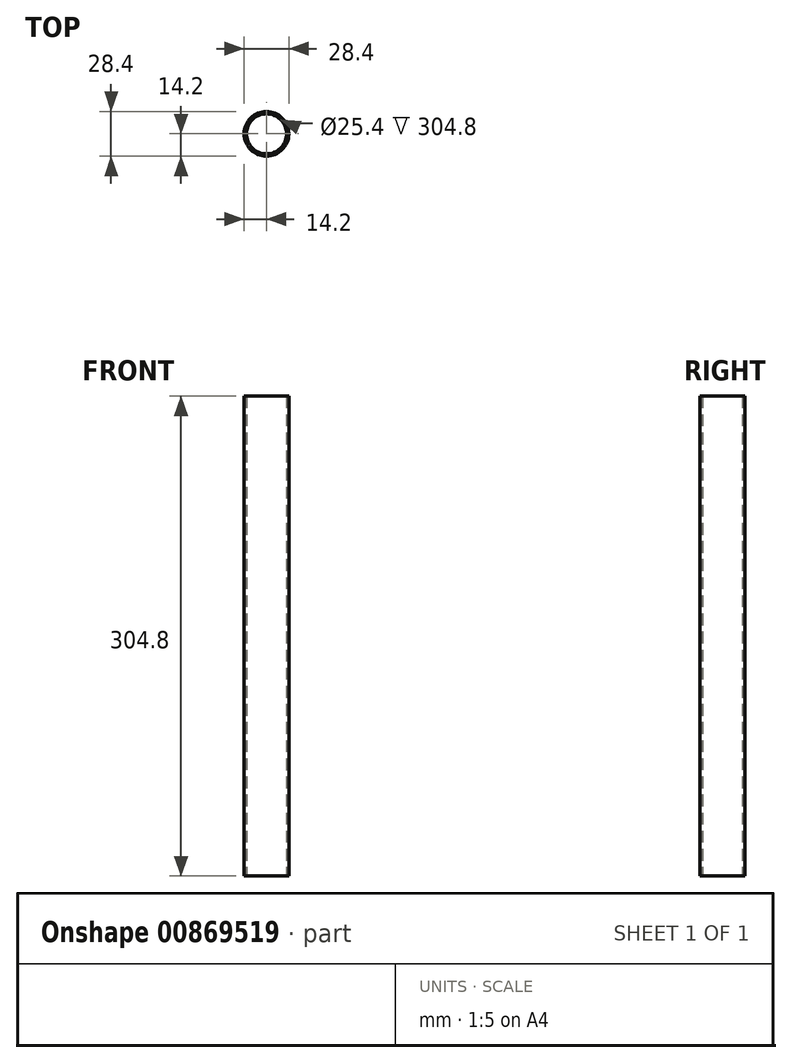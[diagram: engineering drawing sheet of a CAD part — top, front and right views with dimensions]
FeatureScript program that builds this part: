
annotation { "Feature Type Name" : "Feature", "Feature Type Description" : "" }
export const myFeature = defineFeature(function(context is Context, id is Id, definition is map)
    precondition{}
    {
        {
            var Q0;
            Q0=qCreatedBy(makeId("Top.planeOp"),FACE);
            var sketch = newSketch(context, id + "F0", { "sketchPlane" : qUnion([Q0])});
            skCircle(sketch, "E0", {"center": v(0, 0) * mm, "radius": 12.7 * mm});
            skCircle(sketch, "E1.0", {"center": v(0, 0) * mm, "radius": 14.2 * mm});
            skSolve(sketch);
        }
        {
            var Q0;
            Q0 = qSketchRegion(id + "F0", true);
            extrude(context, id + "F1", {"entities" : qUnion([Q0]), "depth" : 304.8 * mm, "offsetDistance" : 25.4 * mm});
        }
    });
